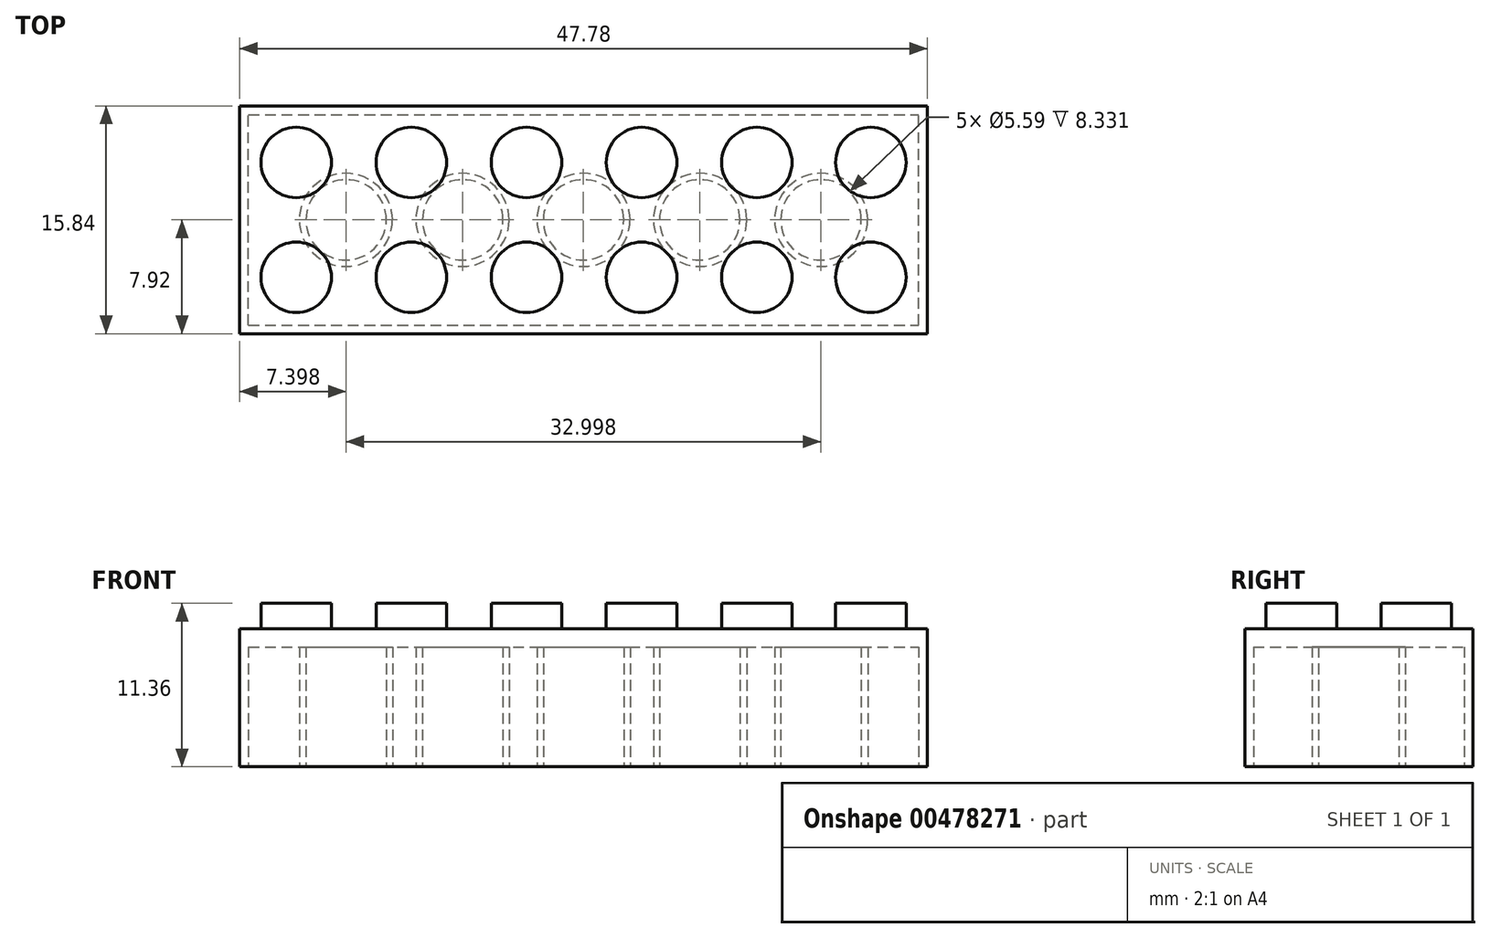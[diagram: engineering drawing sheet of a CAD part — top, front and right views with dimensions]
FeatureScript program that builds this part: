
annotation { "Feature Type Name" : "Feature", "Feature Type Description" : "" }
export const myFeature = defineFeature(function(context is Context, id is Id, definition is map)
    precondition{}
    {
        {
            var Q0;
            Q0=qCreatedBy(makeId("Top.planeOp"),FACE);
            var sketch = newSketch(context, id + "F0", { "sketchPlane" : qUnion([Q0])});
            skLineSegment(sketch, "E0.bottom", {"start": v(-23.89, 7.92) * mm, "end": v(23.89, 7.92) * mm});
            skLineSegment(sketch, "E0.top", {"start": v(-23.89, -7.92) * mm, "end": v(23.89, -7.92) * mm});
            skLineSegment(sketch, "E0.left", {"start": v(-23.89, 7.92) * mm, "end": v(-23.89, -7.92) * mm});
            skLineSegment(sketch, "E0.right", {"start": v(23.89, 7.92) * mm, "end": v(23.89, -7.92) * mm});
            skPoint(sketch, "E0.middle", {"position": v(0, 0) * mm});
            skSolve(sketch);
        }
        {
            var Q0;
            Q0=makeQuery(id+"F0.imprint","IMPRINT",FACE,{"disambiguationData":[TD([[makeQuery(id+"F0.imprint","IMPRINT",EDGE,{"derivedFrom":sQuery(id+"F0.wireOp",EDGE,"E0.bottom")}),-1.0]])]});
            extrude(context, id + "F1", {"entities" : qUnion([Q0]), "endBound" : BoundingType.SYMMETRIC, "depth" : 9.58 * mm});
        }
        {
            var Q0;
            Q0=makeQuery(id+"F1.opExtrude","CAP_FACE",FACE,{"disambiguationData":[OSD([sQuery(id+"F0.wireOp",EDGE,"E0.bottom"),sQuery(id+"F0.wireOp",EDGE,"E0.top"),sQuery(id+"F0.wireOp",EDGE,"E0.left"),sQuery(id+"F0.wireOp",EDGE,"E0.right")])],"isStart":false});
            var sketch = newSketch(context, id + "F2", { "sketchPlane" : qUnion([Q0])});
            skCircle(sketch, "E1", {"center": v(-19.96, 4) * mm, "radius": 2.45 * mm});
            skSolve(sketch);
        }
        {
            var Q0;
            Q0=makeQuery(id+"F2.imprint","IMPRINT",FACE,{"disambiguationData":[TD([[makeQuery(id+"F2.imprint","IMPRINT",EDGE,{"derivedFrom":sQuery(id+"F2.wireOp",EDGE,"E1")}),-1.0]])]});
            var sketch = newSketch(context, id + "F3", { "sketchPlane" : qUnion([Q0])});
            skCircle(sketch, "E2", {"center": v(-11.96, 4) * mm, "radius": 2.45 * mm});
            skSolve(sketch);
        }
        {
            var Q0;
            Q0=makeQuery(id+"F2.imprint","IMPRINT",FACE,{"disambiguationData":[TD([[makeQuery(id+"F2.imprint","IMPRINT",EDGE,{"derivedFrom":sQuery(id+"F2.wireOp",EDGE,"E1")}),-1.0]])]});
            var sketch = newSketch(context, id + "F4", { "sketchPlane" : qUnion([Q0])});
            skCircle(sketch, "E3", {"center": v(-3.96, 4) * mm, "radius": 2.45 * mm});
            skSolve(sketch);
        }
        {
            var Q0;
            Q0=makeQuery(id+"F2.imprint","IMPRINT",FACE,{"disambiguationData":[TD([[makeQuery(id+"F2.imprint","IMPRINT",EDGE,{"derivedFrom":sQuery(id+"F2.wireOp",EDGE,"E1")}),-1.0]])]});
            var sketch = newSketch(context, id + "F5", { "sketchPlane" : qUnion([Q0])});
            skCircle(sketch, "E4", {"center": v(4.04, 4) * mm, "radius": 2.45 * mm});
            skSolve(sketch);
        }
        {
            var Q0;
            Q0=makeQuery(id+"F2.imprint","IMPRINT",FACE,{"disambiguationData":[TD([[makeQuery(id+"F2.imprint","IMPRINT",EDGE,{"derivedFrom":sQuery(id+"F2.wireOp",EDGE,"E1")}),-1.0]])]});
            var sketch = newSketch(context, id + "F6", { "sketchPlane" : qUnion([Q0])});
            skCircle(sketch, "E5", {"center": v(12.04, 4) * mm, "radius": 2.45 * mm});
            skSolve(sketch);
        }
        {
            var Q0;
            Q0=makeQuery(id+"F2.imprint","IMPRINT",FACE,{"disambiguationData":[TD([[makeQuery(id+"F2.imprint","IMPRINT",EDGE,{"derivedFrom":sQuery(id+"F2.wireOp",EDGE,"E1")}),-1.0]])]});
            var sketch = newSketch(context, id + "F7", { "sketchPlane" : qUnion([Q0])});
            skCircle(sketch, "E6", {"center": v(19.96, 4) * mm, "radius": 2.45 * mm});
            skSolve(sketch);
        }
        {
            var Q0;
            Q0=makeQuery(id+"F2.imprint","IMPRINT",FACE,{"disambiguationData":[TD([[makeQuery(id+"F2.imprint","IMPRINT",EDGE,{"derivedFrom":sQuery(id+"F2.wireOp",EDGE,"E1")}),-1.0]])]});
            var sketch = newSketch(context, id + "F8", { "sketchPlane" : qUnion([Q0])});
            skCircle(sketch, "E7", {"center": v(-19.96, -4) * mm, "radius": 2.45 * mm});
            skSolve(sketch);
        }
        {
            var Q0;
            Q0=makeQuery(id+"F2.imprint","IMPRINT",FACE,{"disambiguationData":[TD([[makeQuery(id+"F2.imprint","IMPRINT",EDGE,{"derivedFrom":sQuery(id+"F2.wireOp",EDGE,"E1")}),-1.0]])]});
            var sketch = newSketch(context, id + "F9", { "sketchPlane" : qUnion([Q0])});
            skCircle(sketch, "E8", {"center": v(-11.96, -4) * mm, "radius": 2.45 * mm});
            skSolve(sketch);
        }
        {
            var Q0;
            Q0=makeQuery(id+"F2.imprint","IMPRINT",FACE,{"disambiguationData":[TD([[makeQuery(id+"F2.imprint","IMPRINT",EDGE,{"derivedFrom":sQuery(id+"F2.wireOp",EDGE,"E1")}),-1.0]])]});
            var sketch = newSketch(context, id + "F10", { "sketchPlane" : qUnion([Q0])});
            skCircle(sketch, "E9", {"center": v(-3.96, -4) * mm, "radius": 2.45 * mm});
            skSolve(sketch);
        }
        {
            var Q0;
            Q0=makeQuery(id+"F2.imprint","IMPRINT",FACE,{"disambiguationData":[TD([[makeQuery(id+"F2.imprint","IMPRINT",EDGE,{"derivedFrom":sQuery(id+"F2.wireOp",EDGE,"E1")}),-1.0]])]});
            var sketch = newSketch(context, id + "F11", { "sketchPlane" : qUnion([Q0])});
            skCircle(sketch, "E10", {"center": v(4.04, -4) * mm, "radius": 2.45 * mm});
            skSolve(sketch);
        }
        {
            var Q0;
            Q0=makeQuery(id+"F2.imprint","IMPRINT",FACE,{"disambiguationData":[TD([[makeQuery(id+"F2.imprint","IMPRINT",EDGE,{"derivedFrom":sQuery(id+"F2.wireOp",EDGE,"E1")}),-1.0]])]});
            var sketch = newSketch(context, id + "F12", { "sketchPlane" : qUnion([Q0])});
            skCircle(sketch, "E11", {"center": v(12.04, -4) * mm, "radius": 2.45 * mm});
            skSolve(sketch);
        }
        {
            var Q0;
            Q0=makeQuery(id+"F2.imprint","IMPRINT",FACE,{"disambiguationData":[TD([[makeQuery(id+"F2.imprint","IMPRINT",EDGE,{"derivedFrom":sQuery(id+"F2.wireOp",EDGE,"E1")}),-1.0]])]});
            var sketch = newSketch(context, id + "F13", { "sketchPlane" : qUnion([Q0])});
            skCircle(sketch, "E12", {"center": v(19.96, -4) * mm, "radius": 2.45 * mm});
            skSolve(sketch);
        }
        {
            var Q0;
            Q0=makeQuery(id+"F2.imprint","IMPRINT",FACE,{"disambiguationData":[TD([[makeQuery(id+"F2.imprint","IMPRINT",EDGE,{"derivedFrom":sQuery(id+"F2.wireOp",EDGE,"E1")}),1.0]])]});
            extrude(context, id + "F14", {"entities" : qUnion([Q0]), "operationType" : NewBodyOperationType.ADD, "depth" : 1.78 * mm});
        }
        {
            var Q0;
            Q0=makeQuery(id+"F3.imprint","IMPRINT",FACE,{"disambiguationData":[TD([[makeQuery(id+"F3.imprint","IMPRINT",EDGE,{"derivedFrom":sQuery(id+"F3.wireOp",EDGE,"E2")}),1.0]])]});
            extrude(context, id + "F15", {"entities" : qUnion([Q0]), "operationType" : NewBodyOperationType.ADD, "depth" : 1.78 * mm});
        }
        {
            var Q0;
            Q0=makeQuery(id+"F4.imprint","IMPRINT",FACE,{"disambiguationData":[TD([[makeQuery(id+"F4.imprint","IMPRINT",EDGE,{"derivedFrom":sQuery(id+"F4.wireOp",EDGE,"E3")}),1.0]])]});
            extrude(context, id + "F16", {"entities" : qUnion([Q0]), "operationType" : NewBodyOperationType.ADD, "depth" : 1.78 * mm});
        }
        {
            var Q0;
            Q0=makeQuery(id+"F5.imprint","IMPRINT",FACE,{"disambiguationData":[TD([[makeQuery(id+"F5.imprint","IMPRINT",EDGE,{"derivedFrom":sQuery(id+"F5.wireOp",EDGE,"E4")}),1.0]])]});
            extrude(context, id + "F17", {"entities" : qUnion([Q0]), "operationType" : NewBodyOperationType.ADD, "depth" : 1.78 * mm});
        }
        {
            var Q0;
            Q0=makeQuery(id+"F6.imprint","IMPRINT",FACE,{"disambiguationData":[TD([[makeQuery(id+"F6.imprint","IMPRINT",EDGE,{"derivedFrom":sQuery(id+"F6.wireOp",EDGE,"E5")}),1.0]])]});
            extrude(context, id + "F18", {"entities" : qUnion([Q0]), "operationType" : NewBodyOperationType.ADD, "depth" : 1.78 * mm});
        }
        {
            var Q0;
            Q0=makeQuery(id+"F7.imprint","IMPRINT",FACE,{"disambiguationData":[TD([[makeQuery(id+"F7.imprint","IMPRINT",EDGE,{"derivedFrom":sQuery(id+"F7.wireOp",EDGE,"E6")}),1.0]])]});
            extrude(context, id + "F19", {"entities" : qUnion([Q0]), "operationType" : NewBodyOperationType.ADD, "depth" : 1.78 * mm});
        }
        {
            var Q0;
            Q0=makeQuery(id+"F8.imprint","IMPRINT",FACE,{"disambiguationData":[TD([[makeQuery(id+"F8.imprint","IMPRINT",EDGE,{"derivedFrom":sQuery(id+"F8.wireOp",EDGE,"E7")}),1.0]])]});
            extrude(context, id + "F20", {"entities" : qUnion([Q0]), "operationType" : NewBodyOperationType.ADD, "depth" : 1.78 * mm});
        }
        {
            var Q0;
            Q0=makeQuery(id+"F9.imprint","IMPRINT",FACE,{"disambiguationData":[TD([[makeQuery(id+"F9.imprint","IMPRINT",EDGE,{"derivedFrom":sQuery(id+"F9.wireOp",EDGE,"E8")}),1.0]])]});
            extrude(context, id + "F21", {"entities" : qUnion([Q0]), "operationType" : NewBodyOperationType.ADD, "depth" : 1.78 * mm});
        }
        {
            var Q0;
            Q0=makeQuery(id+"F10.imprint","IMPRINT",FACE,{"disambiguationData":[TD([[makeQuery(id+"F10.imprint","IMPRINT",EDGE,{"derivedFrom":sQuery(id+"F10.wireOp",EDGE,"E9")}),1.0]])]});
            extrude(context, id + "F22", {"entities" : qUnion([Q0]), "operationType" : NewBodyOperationType.ADD, "depth" : 1.78 * mm});
        }
        {
            var Q0;
            Q0=makeQuery(id+"F11.imprint","IMPRINT",FACE,{"disambiguationData":[TD([[makeQuery(id+"F11.imprint","IMPRINT",EDGE,{"derivedFrom":sQuery(id+"F11.wireOp",EDGE,"E10")}),1.0]])]});
            extrude(context, id + "F23", {"entities" : qUnion([Q0]), "operationType" : NewBodyOperationType.ADD, "depth" : 1.78 * mm});
        }
        {
            var Q0;
            Q0=makeQuery(id+"F12.imprint","IMPRINT",FACE,{"disambiguationData":[TD([[makeQuery(id+"F12.imprint","IMPRINT",EDGE,{"derivedFrom":sQuery(id+"F12.wireOp",EDGE,"E11")}),1.0]])]});
            extrude(context, id + "F24", {"entities" : qUnion([Q0]), "operationType" : NewBodyOperationType.ADD, "depth" : 1.78 * mm});
        }
        {
            var Q0;
            Q0=makeQuery(id+"F13.imprint","IMPRINT",FACE,{"disambiguationData":[TD([[makeQuery(id+"F13.imprint","IMPRINT",EDGE,{"derivedFrom":sQuery(id+"F13.wireOp",EDGE,"E12")}),1.0]])]});
            extrude(context, id + "F25", {"entities" : qUnion([Q0]), "operationType" : NewBodyOperationType.ADD, "depth" : 1.78 * mm});
        }
        {
            var Q0;
            Q0=makeQuery(id+"F1.opExtrude","CAP_FACE",FACE,{"disambiguationData":[OSD([sQuery(id+"F0.wireOp",EDGE,"E0.bottom"),sQuery(id+"F0.wireOp",EDGE,"E0.top"),sQuery(id+"F0.wireOp",EDGE,"E0.left"),sQuery(id+"F0.wireOp",EDGE,"E0.right")])],"isStart":true});
            var sketch = newSketch(context, id + "F26", { "sketchPlane" : qUnion([Q0])});
            skLineSegment(sketch, "E13.bottom", {"start": v(-23.28, 7.32) * mm, "end": v(23.28, 7.32) * mm});
            skLineSegment(sketch, "E13.top", {"start": v(-23.28, -7.32) * mm, "end": v(23.28, -7.32) * mm});
            skLineSegment(sketch, "E13.left", {"start": v(-23.28, 7.32) * mm, "end": v(-23.28, -7.32) * mm});
            skLineSegment(sketch, "E13.right", {"start": v(23.28, 7.32) * mm, "end": v(23.28, -7.32) * mm});
            skPoint(sketch, "E13.middle", {"position": v(0, 0) * mm});
            skSolve(sketch);
        }
        {
            var Q0;
            Q0=makeQuery(id+"F1.opExtrude","CAP_FACE",FACE,{"disambiguationData":[OSD([sQuery(id+"F0.wireOp",EDGE,"E0.bottom"),sQuery(id+"F0.wireOp",EDGE,"E0.top"),sQuery(id+"F0.wireOp",EDGE,"E0.left"),sQuery(id+"F0.wireOp",EDGE,"E0.right")])],"isStart":true});
            var sketch = newSketch(context, id + "F27", { "sketchPlane" : qUnion([Q0])});
            skCircle(sketch, "E14", {"center": v(-16.51, 0) * mm, "radius": 3.24 * mm});
            skSolve(sketch);
        }
        {
            var Q0;
            Q0=makeQuery(id+"F26.imprint","IMPRINT",FACE,{"disambiguationData":[TD([[makeQuery(id+"F26.imprint","IMPRINT",EDGE,{"derivedFrom":sQuery(id+"F26.wireOp",EDGE,"E13.bottom")}),-1.0]])]});
            var sketch = newSketch(context, id + "F28", { "sketchPlane" : qUnion([Q0])});
            skCircle(sketch, "E15", {"center": v(-8.4, 0) * mm, "radius": 3.24 * mm});
            skSolve(sketch);
        }
        {
            var Q0;
            Q0=makeQuery(id+"F26.imprint","IMPRINT",FACE,{"disambiguationData":[TD([[makeQuery(id+"F26.imprint","IMPRINT",EDGE,{"derivedFrom":sQuery(id+"F26.wireOp",EDGE,"E13.bottom")}),-1.0]])]});
            var sketch = newSketch(context, id + "F29", { "sketchPlane" : qUnion([Q0])});
            skCircle(sketch, "E16", {"center": v(0, 0) * mm, "radius": 3.24 * mm});
            skSolve(sketch);
        }
        {
            var Q0;
            Q0=makeQuery(id+"F26.imprint","IMPRINT",FACE,{"disambiguationData":[TD([[makeQuery(id+"F26.imprint","IMPRINT",EDGE,{"derivedFrom":sQuery(id+"F26.wireOp",EDGE,"E13.bottom")}),-1.0]])]});
            var sketch = newSketch(context, id + "F30", { "sketchPlane" : qUnion([Q0])});
            skCircle(sketch, "E17", {"center": v(8.1, 0) * mm, "radius": 3.24 * mm});
            skSolve(sketch);
        }
        {
            var Q0;
            Q0=makeQuery(id+"F26.imprint","IMPRINT",FACE,{"disambiguationData":[TD([[makeQuery(id+"F26.imprint","IMPRINT",EDGE,{"derivedFrom":sQuery(id+"F26.wireOp",EDGE,"E13.bottom")}),-1.0]])]});
            var sketch = newSketch(context, id + "F31", { "sketchPlane" : qUnion([Q0])});
            skCircle(sketch, "E18", {"center": v(16.51, 0) * mm, "radius": 3.24 * mm});
            skSolve(sketch);
        }
        {
            var Q0;
            Q0=makeQuery(id+"F26.imprint","IMPRINT",FACE,{"disambiguationData":[TD([[makeQuery(id+"F26.imprint","IMPRINT",EDGE,{"derivedFrom":sQuery(id+"F26.wireOp",EDGE,"E13.bottom")}),-1.0]])]});
            var sketch = newSketch(context, id + "F32", { "sketchPlane" : qUnion([Q0])});
            skCircle(sketch, "E19", {"center": v(-16.5, 0) * mm, "radius": 2.8 * mm});
            skSolve(sketch);
        }
        {
            var Q0;
            Q0=makeQuery(id+"F26.imprint","IMPRINT",FACE,{"disambiguationData":[TD([[makeQuery(id+"F26.imprint","IMPRINT",EDGE,{"derivedFrom":sQuery(id+"F26.wireOp",EDGE,"E13.bottom")}),-1.0]])]});
            var sketch = newSketch(context, id + "F33", { "sketchPlane" : qUnion([Q0])});
            skCircle(sketch, "E20", {"center": v(-8.39, 0) * mm, "radius": 2.8 * mm});
            skSolve(sketch);
        }
        {
            var Q0;
            Q0=makeQuery(id+"F26.imprint","IMPRINT",FACE,{"disambiguationData":[TD([[makeQuery(id+"F26.imprint","IMPRINT",EDGE,{"derivedFrom":sQuery(id+"F26.wireOp",EDGE,"E13.bottom")}),-1.0]])]});
            var sketch = newSketch(context, id + "F34", { "sketchPlane" : qUnion([Q0])});
            skCircle(sketch, "E21", {"center": v(0, 0) * mm, "radius": 2.8 * mm});
            skSolve(sketch);
        }
        {
            var Q0;
            Q0=makeQuery(id+"F26.imprint","IMPRINT",FACE,{"disambiguationData":[TD([[makeQuery(id+"F26.imprint","IMPRINT",EDGE,{"derivedFrom":sQuery(id+"F26.wireOp",EDGE,"E13.bottom")}),-1.0]])]});
            var sketch = newSketch(context, id + "F35", { "sketchPlane" : qUnion([Q0])});
            skCircle(sketch, "E22", {"center": v(8.08, 0) * mm, "radius": 2.8 * mm});
            skSolve(sketch);
        }
        {
            var Q0;
            Q0=makeQuery(id+"F26.imprint","IMPRINT",FACE,{"disambiguationData":[TD([[makeQuery(id+"F26.imprint","IMPRINT",EDGE,{"derivedFrom":sQuery(id+"F26.wireOp",EDGE,"E13.bottom")}),-1.0]])]});
            var sketch = newSketch(context, id + "F36", { "sketchPlane" : qUnion([Q0])});
            skCircle(sketch, "E23", {"center": v(16.5, 0) * mm, "radius": 2.8 * mm});
            skSolve(sketch);
        }
        {
            var Q0;
            Q0=makeQuery(id+"F30.imprint","IMPRINT",FACE,{"disambiguationData":[TD([[makeQuery(id+"F30.imprint","IMPRINT",EDGE,{"derivedFrom":sQuery(id+"F30.wireOp",EDGE,"E17")}),-1.0]])]});
            extrude(context, id + "F37", {"entities" : qUnion([Q0]), "operationType" : NewBodyOperationType.REMOVE, "oppositeDirection" : true, "depth" : 8.33 * mm, "offsetDistance" : 25.4 * mm});
        }
        {
            var Q0;
            Q0 = qSketchRegion(id + "F27", true);
            extrude(context, id + "F38", {"entities" : qUnion([Q0]), "operationType" : NewBodyOperationType.ADD, "oppositeDirection" : true, "depth" : 8.33 * mm, "offsetDistance" : 25.4 * mm});
        }
        {
            var Q0;
            Q0 = qSketchRegion(id + "F32", true);
            extrude(context, id + "F39", {"entities" : qUnion([Q0]), "operationType" : NewBodyOperationType.REMOVE, "oppositeDirection" : true, "depth" : 8.33 * mm, "offsetDistance" : 25.4 * mm});
        }
        {
            var Q0;
            Q0 = qSketchRegion(id + "F28", true);
            extrude(context, id + "F40", {"entities" : qUnion([Q0]), "operationType" : NewBodyOperationType.ADD, "oppositeDirection" : true, "depth" : 8.33 * mm, "offsetDistance" : 25.4 * mm});
        }
        {
            var Q0;
            Q0 = qSketchRegion(id + "F29", true);
            extrude(context, id + "F41", {"entities" : qUnion([Q0]), "operationType" : NewBodyOperationType.ADD, "oppositeDirection" : true, "depth" : 8.33 * mm, "offsetDistance" : 25.4 * mm});
        }
        {
            var Q0;
            Q0 = qSketchRegion(id + "F31", true);
            extrude(context, id + "F42", {"entities" : qUnion([Q0]), "operationType" : NewBodyOperationType.ADD, "oppositeDirection" : true, "depth" : 8.33 * mm, "offsetDistance" : 25.4 * mm});
        }
        {
            var Q0;
            Q0 = qSketchRegion(id + "F33", true);
            extrude(context, id + "F43", {"entities" : qUnion([Q0]), "operationType" : NewBodyOperationType.REMOVE, "oppositeDirection" : true, "depth" : 8.33 * mm, "offsetDistance" : 25.4 * mm});
        }
        {
            var Q0;
            Q0 = qSketchRegion(id + "F34", true);
            extrude(context, id + "F44", {"entities" : qUnion([Q0]), "operationType" : NewBodyOperationType.REMOVE, "oppositeDirection" : true, "depth" : 8.33 * mm, "offsetDistance" : 25.4 * mm});
        }
        {
            var Q0;
            Q0 = qSketchRegion(id + "F35", true);
            extrude(context, id + "F45", {"entities" : qUnion([Q0]), "operationType" : NewBodyOperationType.REMOVE, "oppositeDirection" : true, "depth" : 8.33 * mm, "offsetDistance" : 25.4 * mm});
        }
        {
            var Q0;
            Q0 = qSketchRegion(id + "F36", true);
            extrude(context, id + "F46", {"entities" : qUnion([Q0]), "operationType" : NewBodyOperationType.REMOVE, "oppositeDirection" : true, "depth" : 8.33 * mm, "offsetDistance" : 25.4 * mm});
        }
    });
